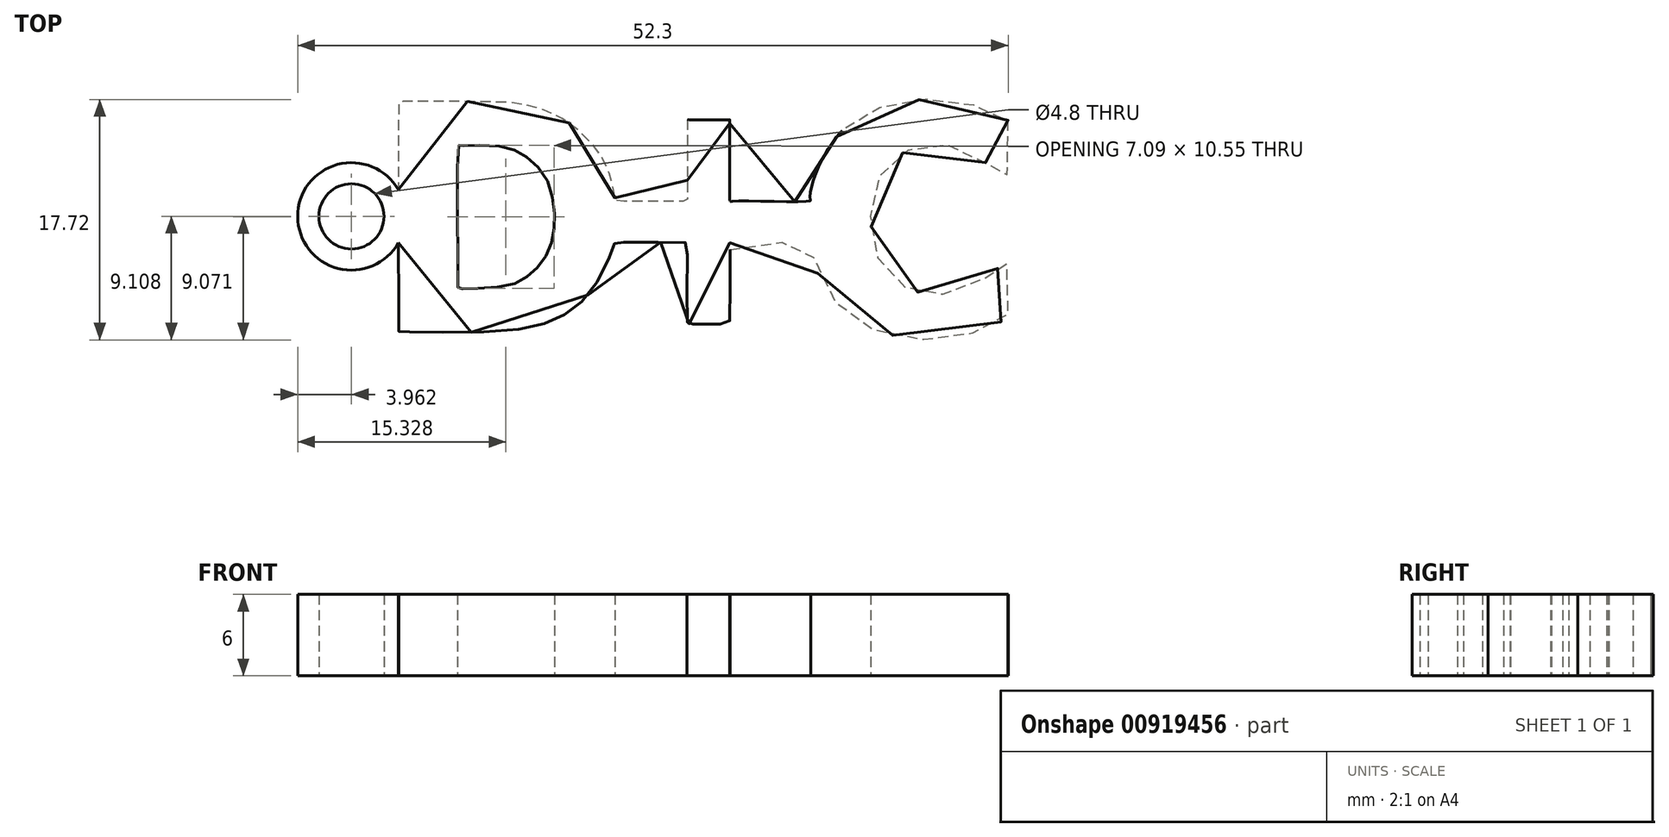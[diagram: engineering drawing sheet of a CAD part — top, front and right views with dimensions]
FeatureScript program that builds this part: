
annotation { "Feature Type Name" : "Feature", "Feature Type Description" : "" }
export const myFeature = defineFeature(function(context is Context, id is Id, definition is map)
    precondition{}
    {
        {
            var Q0;
            Q0=qCreatedBy(makeId("Top.planeOp"),FACE);
            var sketch = newSketch(context, id + "F0", { "sketchPlane" : qUnion([Q0])});
            skFitSpline(sketch, "E0", {"points": [v(-12.2, 6.16) * mm, v(-12.22, -5.12) * mm, v(-12.22, -5.14) * mm, v(-12.2, -5.14) * mm, v(-7.47, -5.13) * mm, v(-4.33, -4.45) * mm, v(-2.6, -2.89) * mm, v(-1.65, -0.86) * mm, v(-1.65, -0.8) * mm, v(-1.58, -0.77) * mm, v(1.89, -0.77) * mm, v(1.93, -0.8) * mm, v(1.93, -4.74) * mm, v(1.94, -4.78) * mm, v(1.98, -4.78) * mm, v(4.02, -4.78) * mm, v(4.02, -4.78) * mm, v(4.01, -0.79) * mm, v(4.02, -0.77) * mm, v(7.98, -0.77) * mm, v(8, -0.79) * mm, v(8.38, -2.38) * mm, v(9.5, -4) * mm, v(11.16, -5.1) * mm, v(13.52, -5.53) * mm, v(15.5, -5.36) * mm, v(17.68, -4.53) * mm, v(17.68, -4.52) * mm, v(17.66, -1.87) * mm, v(17.66, -1.85) * mm, v(17.38, -1.85) * mm, v(17.2, -2.02) * mm, v(15.82, -2.94) * mm, v(14.3, -3.34) * mm, v(13.05, -3.15) * mm, v(11.85, -2.42) * mm, v(11.12, -1.04) * mm, v(10.94, 0.58) * mm, v(11.24, 2.17) * mm, v(11.92, 3.22) * mm, v(13.2, 3.94) * mm, v(14.57, 4.05) * mm, v(16.03, 3.5) * mm, v(17.3, 2.59) * mm, v(17.32, 2.56) * mm, v(17.44, 2.56) * mm, v(17.65, 2.57) * mm, v(17.66, 2.57) * mm, v(17.68, 5.3) * mm, v(17.67, 5.32) * mm, v(16.04, 5.95) * mm, v(13.83, 6.25) * mm, v(12.05, 6.07) * mm, v(10.12, 5.22) * mm, v(9.2, 4.34) * mm, v(8.26, 2.68) * mm, v(7.96, 1.34) * mm, v(7.96, 1.27) * mm, v(4.05, 1.25) * mm, v(4.02, 1.25) * mm, v(4.02, 5.24) * mm, v(4.01, 5.26) * mm, v(3.96, 5.26) * mm, v(1.94, 5.27) * mm, v(1.93, 5.27) * mm, v(1.93, 1.29) * mm, v(1.93, 1.26) * mm, v(1.88, 1.26) * mm, v(-1.58, 1.27) * mm, v(-1.6, 1.28) * mm, v(-1.61, 1.37) * mm, v(-1.89, 2.61) * mm, v(-2.6, 3.91) * mm, v(-4.23, 5.34) * mm, v(-6.14, 6.02) * mm, v(-8.08, 6.14) * mm, v(-12.17, 6.14) * mm, v(-12.2, 6.14) * mm, v(-12.2, 6.16) * mm]});
            skFitSpline(sketch, "E1", {"points": [v(-9.28, 4) * mm, v(-9.32, -3.03) * mm, v(-9.3, -3.05) * mm, v(-8.93, -3.04) * mm, v(-6.94, -2.9) * mm, v(-5.82, -2.37) * mm, v(-5.04, -1.5) * mm, v(-4.65, -0.36) * mm, v(-4.6, 0.94) * mm, v(-5.06, 2.5) * mm, v(-6.09, 3.5) * mm, v(-7.24, 3.95) * mm, v(-9.05, 3.98) * mm, v(-9.25, 3.99) * mm, v(-9.28, 4) * mm]});
            skLineSegment(sketch, "E2", {"start": v(-15.28, 6.14) * mm, "end": v(-15.28, -5.12) * mm, "construction": true});
            skPoint(sketch, "E3.centerSnap0", {"position": v(-15.28, 0.51) * mm});
            skLineSegment(sketch, "E4", {"start": v(-18.43, 0.51) * mm, "end": v(-12.25, 0.51) * mm, "construction": true});
            skCircle(sketch, "E5", {"center": v(-14.55, 0.51) * mm, "radius": 2.64 * mm});
            skCircle(sketch, "E6", {"center": v(-14.55, 0.51) * mm, "radius": 1.6 * mm});
            skSolve(sketch);
        }
        {
            var Q0;
            {var subQ0=sQuery(id+"F0.wireOp",EDGE,"E5");var subQ1=sQuery(id+"F0.wireOp",EDGE,"E0");var subQ2=makeQuery(id+"F0.imprint","INTERSECT",VERTEX,{"disambiguationData":[OD(0.0)],"derivedFrom":[subQ1,subQ0]});Q0=makeQuery(id+"F0.imprint","IMPRINT",FACE,{"disambiguationData":[TD([[makeQuery(id+"F0.imprint","IMPRINT",EDGE,{"disambiguationData":[TD([[subQ2,1.0]])],"derivedFrom":subQ1}),1.0]])]});}
            var Q1;
            Q1=makeQuery(id+"F0.imprint","IMPRINT",FACE,{"disambiguationData":[TD([[makeQuery(id+"F0.imprint","IMPRINT",EDGE,{"derivedFrom":sQuery(id+"F0.wireOp",EDGE,"E6")}),-1.0]])]});
            var Q2;
            Q2=makeQuery(id+"F0.imprint","IMPRINT",FACE,{"disambiguationData":[TD([[makeQuery(id+"F0.imprint","IMPRINT",EDGE,{"derivedFrom":sQuery(id+"F0.wireOp",EDGE,"E1")}),-1.0]])]});
            extrude(context, id + "F1", {"entities" : qUnion([Q0, Q1, Q2]), "depth" : 4 * mm, "offsetDistance" : 25 * mm});
        }
        {
            var Q0;
            Q0=makeQuery(id+"F1.opExtrude","SWEPT_BODY",BODY,{"disambiguationData":[OSD([sQuery(id+"F0.wireOp",EDGE,"E0"),sQuery(id+"F0.wireOp",EDGE,"E1"),sQuery(id+"F0.wireOp",EDGE,"E5"),sQuery(id+"F0.wireOp",EDGE,"E6")])]});
            var Q1;
            Q1=qCreatedBy(makeId("Origin.pointOp"),VERTEX);
            transform(context, id + "F2", {"entities" : qUnion([Q0]), "transformType" : TransformType.SCALE_UNIFORMLY, "scale" : 1.5, "scalePoint" : qUnion([Q1]), "makeCopy" : false});
        }
    });
